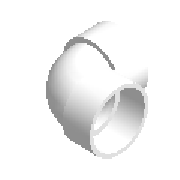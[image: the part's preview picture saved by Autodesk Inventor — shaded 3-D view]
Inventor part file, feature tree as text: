
AUTODESK INVENTOR PART (.ipt)
format: ipt  version: 2023.1 (Build 271208000, 208)  size: 239,616 bytes
history: native  units: mm (DEFAULTED — no unit token found)
features: other x6, sketch x4
ambient origin geometry x8: Origin, YZ Plane, XZ Plane, XY Plane, X Axis, Y Axis, Z Axis, Center Point
bodies: Solid1 (feature_tree)
feature tree (10):
  other  "Work Point1"
  other  "Work Point2"
  other  "Work Axis1"
  other  "Work Point3"
  other  "Work Axis2"
  other  "Work Point4"
  sketch  "Sketch1"  dims[d1=89.45mm]
  sketch  "Sketch2"  dims[d2=88.65mm]
  sketch  "Sketch3"  dims[d0=89.45mm]
  sketch  "Sketch4"  dims[d3=88.65mm d4=3.4mm d5=40.0mm d6=3.4mm d7=77.2mm d39=90.0deg d8=77.2mm d9=3.6mm d10=44.6mm d11=44.6mm d12=44.6mm d13=0.0mm d14=3.6mm d15=40.0mm d16=3.4mm d17=89.45mm d18=88.65mm d19=77.2mm d82=90.0deg d83=0.0mm]
